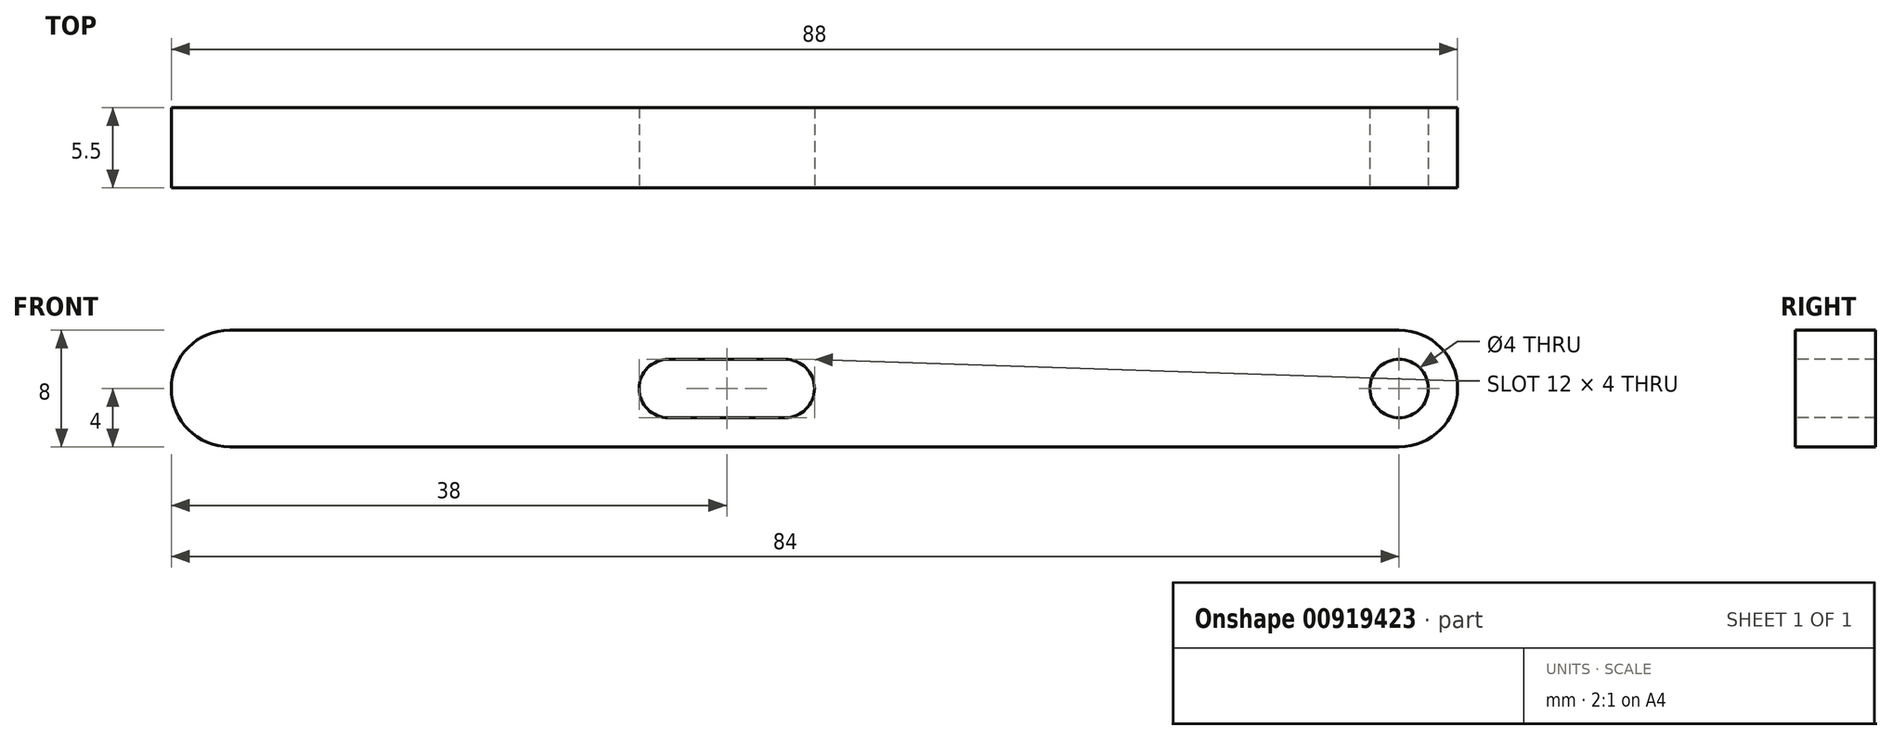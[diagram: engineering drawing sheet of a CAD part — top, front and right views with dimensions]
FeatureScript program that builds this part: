
annotation { "Feature Type Name" : "Feature", "Feature Type Description" : "" }
export const myFeature = defineFeature(function(context is Context, id is Id, definition is map)
    precondition{}
    {
        {
            var Q0;
            Q0=qCreatedBy(makeId("Front.planeOp"),FACE);
            var sketch = newSketch(context, id + "F0", { "sketchPlane" : qUnion([Q0])});
            skCircle(sketch, "E0", {"center": v(0, 0) * mm, "radius": 4 * mm});
            skCircle(sketch, "E1", {"center": v(-80, 0) * mm, "radius": 4 * mm});
            skLineSegment(sketch, "E2", {"start": v(-80, 4) * mm, "end": v(0, 4) * mm});
            skLineSegment(sketch, "E3", {"start": v(-80, -4) * mm, "end": v(0, -4) * mm});
            skSolve(sketch);
        }
        {
            var Q0;
            {var subQ0=sQuery(id+"F0.wireOp",EDGE,"E2");Q0=makeQuery(id+"F0.imprint","IMPRINT",FACE,{"disambiguationData":[TD([[makeQuery(id+"F0.imprint","IMPRINT",EDGE,{"derivedFrom":subQ0}),-1.0]])]});}
            var Q1;
            {var subQ0=sQuery(id+"F0.wireOp",EDGE,"E1");var subQ1=makeQuery(id+"F0.imprint","INTERSECT",VERTEX,{"derivedFrom":[subQ0,sQuery(id+"F0.wireOp",EDGE,"E2")]});Q1=makeQuery(id+"F0.imprint","IMPRINT",FACE,{"disambiguationData":[TD([[makeQuery(id+"F0.imprint","IMPRINT",EDGE,{"disambiguationData":[TD([[subQ1,-1.0]])],"derivedFrom":subQ0}),1.0]])]});}
            var Q2;
            {var subQ0=sQuery(id+"F0.wireOp",EDGE,"E0");var subQ1=makeQuery(id+"F0.imprint","INTERSECT",VERTEX,{"derivedFrom":[subQ0,sQuery(id+"F0.wireOp",EDGE,"E2")]});Q2=makeQuery(id+"F0.imprint","IMPRINT",FACE,{"disambiguationData":[TD([[makeQuery(id+"F0.imprint","IMPRINT",EDGE,{"disambiguationData":[TD([[subQ1,-1.0]])],"derivedFrom":subQ0}),1.0]])]});}
            extrude(context, id + "F1", {"entities" : qUnion([Q0, Q1, Q2]), "depth" : 5.5 * mm, "offsetDistance" : 25 * mm});
        }
        {
            var Q0;
            Q0=makeQuery(id+"F1.opExtrude","CAP_FACE",FACE,{"disambiguationData":[OSD([sQuery(id+"F0.wireOp",EDGE,"E0"),sQuery(id+"F0.wireOp",EDGE,"E1"),sQuery(id+"F0.wireOp",EDGE,"E2"),sQuery(id+"F0.wireOp",EDGE,"E3")])],"isStart":false});
            var sketch = newSketch(context, id + "F2", { "sketchPlane" : qUnion([Q0])});
            skCircle(sketch, "E4", {"center": v(0, 0) * mm, "radius": 2 * mm});
            skCircle(sketch, "E5", {"center": v(-50, 0) * mm, "radius": 2 * mm});
            skCircle(sketch, "E6", {"center": v(-42, 0) * mm, "radius": 2 * mm});
            skLineSegment(sketch, "E7", {"start": v(-50, 2) * mm, "end": v(-42, 2) * mm});
            skLineSegment(sketch, "E8", {"start": v(-50, -2) * mm, "end": v(-42, -2) * mm});
            skSolve(sketch);
        }
        {
            var Q0;
            Q0=makeQuery(id+"F2.imprint","IMPRINT",FACE,{"disambiguationData":[TD([[makeQuery(id+"F2.imprint","IMPRINT",EDGE,{"derivedFrom":sQuery(id+"F2.wireOp",EDGE,"E4")}),1.0]])]});
            var Q1;
            {var subQ0=sQuery(id+"F2.wireOp",EDGE,"E7");Q1=makeQuery(id+"F2.imprint","IMPRINT",FACE,{"disambiguationData":[TD([[makeQuery(id+"F2.imprint","IMPRINT",EDGE,{"derivedFrom":subQ0}),-1.0]])]});}
            var Q2;
            {var subQ0=sQuery(id+"F2.wireOp",EDGE,"E6");var subQ1=makeQuery(id+"F2.imprint","INTERSECT",VERTEX,{"derivedFrom":[subQ0,sQuery(id+"F2.wireOp",EDGE,"E7")]});Q2=makeQuery(id+"F2.imprint","IMPRINT",FACE,{"disambiguationData":[TD([[makeQuery(id+"F2.imprint","IMPRINT",EDGE,{"disambiguationData":[TD([[subQ1,-1.0]])],"derivedFrom":subQ0}),1.0]])]});}
            var Q3;
            {var subQ0=sQuery(id+"F2.wireOp",EDGE,"E5");var subQ1=makeQuery(id+"F2.imprint","INTERSECT",VERTEX,{"derivedFrom":[subQ0,sQuery(id+"F2.wireOp",EDGE,"E7")]});Q3=makeQuery(id+"F2.imprint","IMPRINT",FACE,{"disambiguationData":[TD([[makeQuery(id+"F2.imprint","IMPRINT",EDGE,{"disambiguationData":[TD([[subQ1,-1.0]])],"derivedFrom":subQ0}),1.0]])]});}
            extrude(context, id + "F3", {"entities" : qUnion([Q0, Q1, Q2, Q3]), "operationType" : NewBodyOperationType.REMOVE, "oppositeDirection" : true, "depth" : 25 * mm, "offsetDistance" : 25 * mm});
        }
    });
